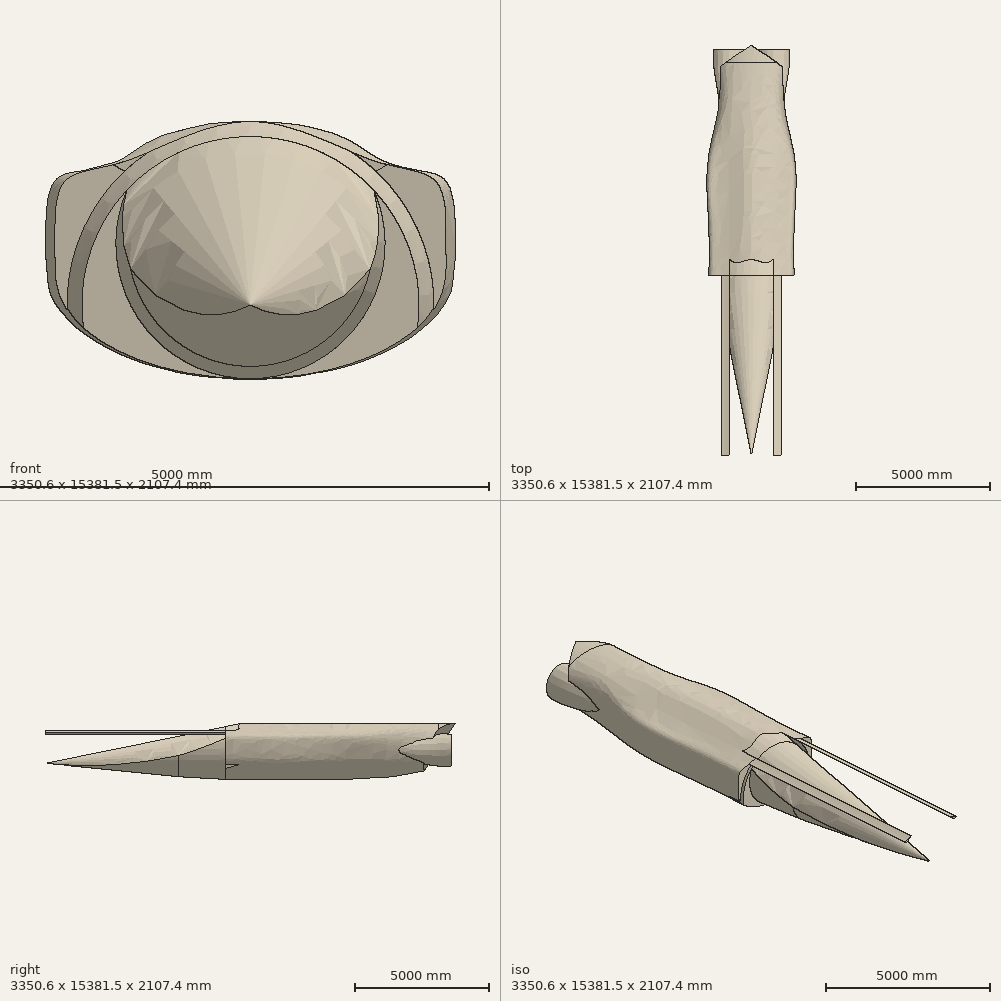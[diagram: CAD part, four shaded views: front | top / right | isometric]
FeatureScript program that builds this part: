
annotation { "Feature Type Name" : "Feature", "Feature Type Description" : "" }
export const myFeature = defineFeature(function(context is Context, id is Id, definition is map)
    precondition{}
    {
        {
            var Q0;
            Q0=qCreatedBy(makeId("Front.planeOp"),FACE);
            cPlane(context, id + "F0", {"entities" : qUnion([Q0]), "cplaneType" : CPlaneType.OFFSET, "offset" : 1750 * mm, "width" : 152.4 * mm, "height" : 152.4 * mm});
        }
        {
            var Q0;
            Q0=qCreatedBy(id+"F0.planeOp",FACE);
            var sketch = newSketch(context, id + "F1", { "sketchPlane" : qUnion([Q0])});
            skPoint(sketch, "E0.middle", {"position": v(0, 0) * mm});
            skFitSpline(sketch, "E1", {"points": [v(0, 1000) * mm, v(1060, 662.5) * mm, v(1517.6, 506.84) * mm, v(1600, 0) * mm, v(1517.6, -506.84) * mm, v(750, -1000) * mm, v(-750, -1000) * mm, v(-1517.6, -506.84) * mm, v(-1600, 0) * mm, v(-1517.6, 506.84) * mm, v(-1060, 662.5) * mm, v(0, 1000) * mm]});
            skSolve(sketch);
        }
        {
            var Q0;
            Q0=qCreatedBy(makeId("Front.planeOp"),FACE);
            var sketch = newSketch(context, id + "F2", { "sketchPlane" : qUnion([Q0])});
            skPoint(sketch, "E2.middle", {"position": v(0, 0) * mm});
            skFitSpline(sketch, "E3", {"points": [v(0, 1000) * mm, v(1060, 662.5) * mm, v(1517.6, 506.84) * mm, v(1600, 0) * mm, v(1517.6, -506.84) * mm, v(750, -1000) * mm, v(-750, -1000) * mm, v(-1517.6, -506.84) * mm, v(-1600, 0) * mm, v(-1517.6, 506.84) * mm, v(-1060, 662.5) * mm, v(0, 1000) * mm]});
            skSolve(sketch);
        }
        {
            var Q0;
            Q0=qCreatedBy(makeId("Front.planeOp"),FACE);
            cPlane(context, id + "F3", {"entities" : qUnion([Q0]), "cplaneType" : CPlaneType.OFFSET, "offset" : 2800 * mm, "oppositeDirection" : true, "width" : 150 * mm, "height" : 150 * mm});
        }
        {
            var Q0;
            Q0=qCreatedBy(id+"F3.planeOp",FACE);
            var sketch = newSketch(context, id + "F4", { "sketchPlane" : qUnion([Q0])});
            skPoint(sketch, "E4.middle", {"position": v(0, 0) * mm});
            skFitSpline(sketch, "E5", {"points": [v(0, 1000) * mm, v(1060, 662.5) * mm, v(1517.6, 506.84) * mm, v(1600, 0) * mm, v(1517.6, -506.84) * mm, v(750, -1000) * mm, v(-750, -1000) * mm, v(-1517.6, -506.84) * mm, v(-1600, 0) * mm, v(-1517.6, 506.84) * mm, v(-1060, 662.5) * mm, v(0, 1000) * mm]});
            skSolve(sketch);
        }
        {
            var Q0;
            Q0=qCreatedBy(makeId("Front.planeOp"),FACE);
            cPlane(context, id + "F5", {"entities" : qUnion([Q0]), "cplaneType" : CPlaneType.OFFSET, "offset" : 4500 * mm, "oppositeDirection" : true, "width" : 150 * mm, "height" : 150 * mm});
        }
        {
            var Q0;
            Q0=qCreatedBy(id+"F5.planeOp",FACE);
            var sketch = newSketch(context, id + "F6", { "sketchPlane" : qUnion([Q0])});
            skPoint(sketch, "E6.middle", {"position": v(0, 0) * mm});
            skFitSpline(sketch, "E7", {"points": [v(0, 1000) * mm, v(1060, 662.5) * mm, v(1250, 0) * mm, v(1060, -662.5) * mm, v(0, -1000) * mm, v(-1060, -662.5) * mm, v(-1250, 0) * mm, v(-1060, 662.5) * mm, v(0, 1000) * mm]});
            skSolve(sketch);
        }
        {
            var Q0;
            Q0=qCreatedBy(makeId("Front.planeOp"),FACE);
            cPlane(context, id + "F7", {"entities" : qUnion([Q0]), "cplaneType" : CPlaneType.OFFSET, "offset" : 6232.05 * mm, "oppositeDirection" : true, "width" : 150 * mm, "height" : 150 * mm});
        }
        {
            var Q0;
            Q0=qCreatedBy(id+"F7.planeOp",FACE);
            var sketch = newSketch(context, id + "F8", { "sketchPlane" : qUnion([Q0])});
            skPoint(sketch, "E8.middle", {"position": v(0, 0) * mm});
            skFitSpline(sketch, "E9", {"points": [v(0, 1000) * mm, v(1060, 662.5) * mm, v(1250, 0) * mm, v(848, -530) * mm, v(-848, -530) * mm, v(-1250, 0) * mm, v(-1060, 662.5) * mm, v(0, 1000) * mm]});
            skSolve(sketch);
        }
        {
            var Q0;
            Q0 = qSketchRegion(id + "F1", true);
            var Q1;
            Q1 = qSketchRegion(id + "F2", true);
            var Q2;
            Q2 = qSketchRegion(id + "F4", true);
            var Q3;
            Q3 = qSketchRegion(id + "F6", true);
            var Q4;
            Q4 = qSketchRegion(id + "F8", true);
            loft(context, id + "F9", {"sheetProfilesArray" : [{ "sheetProfileEntities" : qUnion([Q0]) }, { "sheetProfileEntities" : qUnion([Q1]) }, { "sheetProfileEntities" : qUnion([Q2]) }, { "sheetProfileEntities" : qUnion([Q3]) }, { "sheetProfileEntities" : qUnion([Q4]) }]});
        }
        {
            var Q0;
            Q0=makeQuery(id+"F9.opLoft","CAP_FACE",FACE,{"disambiguationData":[OSD([makeQuery(id+"F8.imprint","IMPRINT",FACE,{"disambiguationData":[TD([[makeQuery(id+"F8.imprint","IMPRINT",EDGE,{"derivedFrom":sQuery(id+"F8.wireOp",EDGE,"E9")}),-1.0]])]})])],"isStart":true});
            extrude(context, id + "F10", {"entities" : qUnion([Q0]), "operationType" : NewBodyOperationType.ADD, "depth" : 649.4 * mm});
        }
        {
            var Q0;
            Q0=qCreatedBy(makeId("Right.planeOp"),FACE);
            var sketch = newSketch(context, id + "F11", { "sketchPlane" : qUnion([Q0])});
            skLineSegment(sketch, "E10", {"start": v(0, 0) * mm, "end": v(4500, 0) * mm});
            skLineSegment(sketch, "E11", {"start": v(4500, 0) * mm, "end": v(6232.05, 0) * mm});
            skLineSegment(sketch, "E12", {"start": v(4500, 0) * mm, "end": v(4500, 1000) * mm});
            skLineSegment(sketch, "E13", {"start": v(4500, 1000) * mm, "end": v(6881.46, 1000) * mm});
            skLineSegment(sketch, "E14", {"start": v(6881.46, 1000) * mm, "end": v(6881.46, -1000) * mm});
            skLineSegment(sketch, "E15", {"start": v(6881.46, 1000) * mm, "end": v(6232.05, 0) * mm});
            skLineSegment(sketch, "E16", {"start": v(6232.05, 0) * mm, "end": v(5582.64, -1000) * mm});
            skLineSegment(sketch, "E17", {"start": v(5582.64, -1000) * mm, "end": v(6881.46, -1000) * mm});
            skSolve(sketch);
        }
        {
            var Q0;
            Q0=makeQuery(id+"F11.imprint","IMPRINT",FACE,{"disambiguationData":[TD([[makeQuery(id+"F11.imprint","IMPRINT",EDGE,{"derivedFrom":sQuery(id+"F11.wireOp",EDGE,"E14")}),-1.0]])]});
            var Q1;
            Q1=sQuery(id+"F11.wireOp",EDGE,"E13");
            revolve(context, id + "F12", {"operationType" : NewBodyOperationType.REMOVE, "entities" : qUnion([Q0]), "axis" : qUnion([Q1]), "revolveType" : RevolveType.SYMMETRIC, "oppositeDirection" : true, "angle" : 182 * degree});
        }
        {
            var Q0;
            Q0=makeQuery(id+"F9.opLoft","CAP_FACE",FACE,{"disambiguationData":[OSD([makeQuery(id+"F1.imprint","IMPRINT",FACE,{"disambiguationData":[TD([[makeQuery(id+"F1.imprint","IMPRINT",EDGE,{"derivedFrom":sQuery(id+"F1.wireOp",EDGE,"E1")}),-1.0]])]})])],"isStart":true});
            extrude(context, id + "F13", {"entities" : qUnion([Q0]), "depth" : 6750 * mm});
        }
        {
            var Q0;
            Q0=qCreatedBy(makeId("Right.planeOp"),FACE);
            var sketch = newSketch(context, id + "F14", { "sketchPlane" : qUnion([Q0])});
            skLineSegment(sketch, "E18", {"start": v(0, 0) * mm, "end": v(-3500, 0) * mm});
            skLineSegment(sketch, "E19", {"start": v(-3500, 0) * mm, "end": v(-3500, -1000) * mm});
            skLineSegment(sketch, "E20", {"start": v(-3500, -1000) * mm, "end": v(-8500, -1000) * mm});
            skLineSegment(sketch, "E21", {"start": v(-8500, -1000) * mm, "end": v(-8500, -499.31) * mm});
            skLineSegment(sketch, "E22", {"start": v(-1151.4, 0) * mm, "end": v(-1151.4, 1000) * mm});
            skLineSegment(sketch, "E23", {"start": v(-1151.4, 1000) * mm, "end": v(-8500, -499.31) * mm});
            skLineSegment(sketch, "E24", {"start": v(-8500, -499.31) * mm, "end": v(-3500, -1000) * mm});
            skLineSegment(sketch, "E25", {"start": v(-1151.4, 1000) * mm, "end": v(-8500, 1000) * mm});
            skLineSegment(sketch, "E26", {"start": v(-8500, 1000) * mm, "end": v(-8500, -499.31) * mm});
            skLineSegment(sketch, "E27", {"start": v(-8500, -1000) * mm, "end": v(-8500, -1750) * mm});
            skLineSegment(sketch, "E28", {"start": v(-8500, -1750) * mm, "end": v(-1750, -1750) * mm});
            skPoint(sketch, "E28.endSnap0", {"position": v(-1750, 0) * mm});
            skLineSegment(sketch, "E29", {"start": v(-1750, 0) * mm, "end": v(-1750, -1099.92) * mm});
            skLineSegment(sketch, "E30", {"start": v(-1750, -1099.92) * mm, "end": v(-3500, -1000) * mm});
            skLineSegment(sketch, "E31", {"start": v(-1750, -1099.92) * mm, "end": v(-1750, -1750) * mm});
            skLineSegment(sketch, "E32", {"start": v(-8500, -499.31) * mm, "end": v(-3500, -499.31) * mm});
            skSolve(sketch);
        }
        {
            var Q0;
            Q0=makeQuery(id+"F14.imprint","IMPRINT",FACE,{"disambiguationData":[TD([[makeQuery(id+"F14.imprint","IMPRINT",EDGE,{"derivedFrom":sQuery(id+"F14.wireOp",EDGE,"E23")}),-1.0]])]});
            var Q1;
            Q1=sQuery(id+"F14.wireOp",EDGE,"E32");
            revolve(context, id + "F15", {"operationType" : NewBodyOperationType.REMOVE, "entities" : qUnion([Q0]), "axis" : qUnion([Q1]), "revolveType" : RevolveType.SYMMETRIC, "oppositeDirection" : true, "angle" : 250 * degree});
        }
        {
            var Q0;
            Q0=makeQuery(id+"F14.imprint","IMPRINT",FACE,{"disambiguationData":[TD([[makeQuery(id+"F14.imprint","IMPRINT",EDGE,{"derivedFrom":sQuery(id+"F14.wireOp",EDGE,"E20")}),-1.0]])]});
            var Q1;
            Q1=makeQuery(id+"F14.imprint","IMPRINT",FACE,{"disambiguationData":[TD([[makeQuery(id+"F14.imprint","IMPRINT",EDGE,{"derivedFrom":sQuery(id+"F14.wireOp",EDGE,"E20")}),1.0]])]});
            var Q2;
            Q2=sQuery(id+"F14.wireOp",EDGE,"E18");
            revolve(context, id + "F16", {"operationType" : NewBodyOperationType.REMOVE, "entities" : qUnion([Q0, Q1]), "axis" : qUnion([Q2]), "revolveType" : RevolveType.SYMMETRIC, "oppositeDirection" : true, "angle" : 240 * degree});
        }
        {
            var Q0;
            Q0=qCreatedBy(makeId("Front.planeOp"),FACE);
            cPlane(context, id + "F17", {"entities" : qUnion([Q0]), "cplaneType" : CPlaneType.OFFSET, "offset" : 3500 * mm, "oppositeDirection" : true, "width" : 150 * mm, "height" : 150 * mm});
        }
        {
            var Q0;
            Q0=qCreatedBy(id+"F17.planeOp",FACE);
            var sketch = newSketch(context, id + "F18", { "sketchPlane" : qUnion([Q0])});
            skCircle(sketch, "E33", {"center": v(-825, 0) * mm, "radius": 600 * mm});
            skCircle(sketch, "E34", {"center": v(825, 0) * mm, "radius": 600 * mm});
            skSolve(sketch);
        }
        {
            var Q0;
            Q0=qCreatedBy(makeId("Front.planeOp"),FACE);
            cPlane(context, id + "F19", {"entities" : qUnion([Q0]), "cplaneType" : CPlaneType.OFFSET, "offset" : 4500 * mm, "oppositeDirection" : true, "width" : 150 * mm, "height" : 150 * mm});
        }
        {
            var Q0;
            Q0=qCreatedBy(id+"F19.planeOp",FACE);
            var sketch = newSketch(context, id + "F20", { "sketchPlane" : qUnion([Q0])});
            skCircle(sketch, "E35", {"center": v(-825, 0) * mm, "radius": 400 * mm});
            skCircle(sketch, "E36", {"center": v(825, 0) * mm, "radius": 400 * mm});
            skSolve(sketch);
        }
        {
            var Q0;
            Q0=qCreatedBy(makeId("Front.planeOp"),FACE);
            cPlane(context, id + "F21", {"entities" : qUnion([Q0]), "cplaneType" : CPlaneType.OFFSET, "offset" : 6232.05 * mm, "oppositeDirection" : true, "width" : 150 * mm, "height" : 150 * mm});
        }
        {
            var Q0;
            Q0=qCreatedBy(id+"F21.planeOp",FACE);
            var sketch = newSketch(context, id + "F22", { "sketchPlane" : qUnion([Q0])});
            skCircle(sketch, "E37", {"center": v(-825, 0) * mm, "radius": 600 * mm});
            skCircle(sketch, "E38", {"center": v(825, 0) * mm, "radius": 600 * mm});
            skSolve(sketch);
        }
        {
            var Q0;
            Q0=qCreatedBy(makeId("Front.planeOp"),FACE);
            cPlane(context, id + "F23", {"entities" : qUnion([Q0]), "cplaneType" : CPlaneType.OFFSET, "offset" : 6732.05 * mm, "oppositeDirection" : true, "width" : 150 * mm, "height" : 150 * mm});
        }
        {
            var Q0;
            Q0=qCreatedBy(id+"F23.planeOp",FACE);
            var sketch = newSketch(context, id + "F24", { "sketchPlane" : qUnion([Q0])});
            skCircle(sketch, "E39", {"center": v(-825, 0) * mm, "radius": 600 * mm});
            skCircle(sketch, "E40", {"center": v(825, 0) * mm, "radius": 600 * mm});
            skSolve(sketch);
        }
        {
            var Q0;
            Q0=makeQuery(id+"F18.imprint","IMPRINT",FACE,{"disambiguationData":[TD([[makeQuery(id+"F18.imprint","IMPRINT",EDGE,{"derivedFrom":sQuery(id+"F18.wireOp",EDGE,"E33")}),1.0]])]});
            var Q1;
            Q1=makeQuery(id+"F20.imprint","IMPRINT",FACE,{"disambiguationData":[TD([[makeQuery(id+"F20.imprint","IMPRINT",EDGE,{"derivedFrom":sQuery(id+"F20.wireOp",EDGE,"E35")}),1.0]])]});
            var Q2;
            Q2=makeQuery(id+"F22.imprint","IMPRINT",FACE,{"disambiguationData":[TD([[makeQuery(id+"F22.imprint","IMPRINT",EDGE,{"derivedFrom":sQuery(id+"F22.wireOp",EDGE,"E37")}),1.0]])]});
            var Q3;
            Q3=makeQuery(id+"F24.imprint","IMPRINT",FACE,{"disambiguationData":[TD([[makeQuery(id+"F24.imprint","IMPRINT",EDGE,{"derivedFrom":sQuery(id+"F24.wireOp",EDGE,"E39")}),1.0]])]});
            loft(context, id + "F25", {"sheetProfilesArray" : [{ "sheetProfileEntities" : qUnion([Q0]) }, { "sheetProfileEntities" : qUnion([Q1]) }, { "sheetProfileEntities" : qUnion([Q2]) }, { "sheetProfileEntities" : qUnion([Q3]) }]});
        }
        {
            var Q0;
            Q0=makeQuery(id+"F18.imprint","IMPRINT",FACE,{"disambiguationData":[TD([[makeQuery(id+"F18.imprint","IMPRINT",EDGE,{"derivedFrom":sQuery(id+"F18.wireOp",EDGE,"E34")}),1.0]])]});
            var Q1;
            Q1=makeQuery(id+"F20.imprint","IMPRINT",FACE,{"disambiguationData":[TD([[makeQuery(id+"F20.imprint","IMPRINT",EDGE,{"derivedFrom":sQuery(id+"F20.wireOp",EDGE,"E36")}),1.0]])]});
            var Q2;
            Q2=makeQuery(id+"F22.imprint","IMPRINT",FACE,{"disambiguationData":[TD([[makeQuery(id+"F22.imprint","IMPRINT",EDGE,{"derivedFrom":sQuery(id+"F22.wireOp",EDGE,"E38")}),1.0]])]});
            var Q3;
            Q3=makeQuery(id+"F24.imprint","IMPRINT",FACE,{"disambiguationData":[TD([[makeQuery(id+"F24.imprint","IMPRINT",EDGE,{"derivedFrom":sQuery(id+"F24.wireOp",EDGE,"E40")}),1.0]])]});
            loft(context, id + "F26", {"sheetProfilesArray" : [{ "sheetProfileEntities" : qUnion([Q0]) }, { "sheetProfileEntities" : qUnion([Q1]) }, { "sheetProfileEntities" : qUnion([Q2]) }, { "sheetProfileEntities" : qUnion([Q3]) }]});
        }
    });
